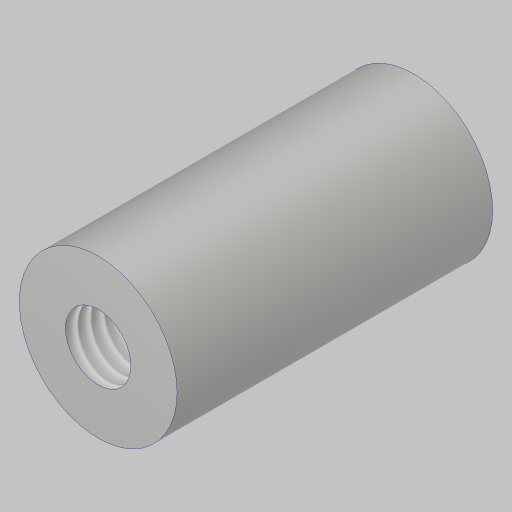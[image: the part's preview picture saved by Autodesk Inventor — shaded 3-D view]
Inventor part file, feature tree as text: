
AUTODESK INVENTOR PART (.ipt)
format: ipt  version: 2023.5 (Build 275446000, 446)  size: 124,928 bytes
history: native  units: in
note: dims shown in document units (in); Inventor stores cm internally (conversion verified against a paired STEP export)
features: extrude x1, hole x1
ambient origin geometry x8: Origin, YZ Plane, XZ Plane, XY Plane, X Axis, Y Axis, Z Axis, Center Point
bodies: Solid1 (feature_tree)
feature tree (2):
  extrude  "Extrusion1"  Depth=0.75in
  hole  "Hole1"  [1 undecoded]
note: 1 required parameter value undecoded (feature->parameter linkage not recoverable at this tier; creation-order binding heuristic only, values carry confidence <= 0.55)
